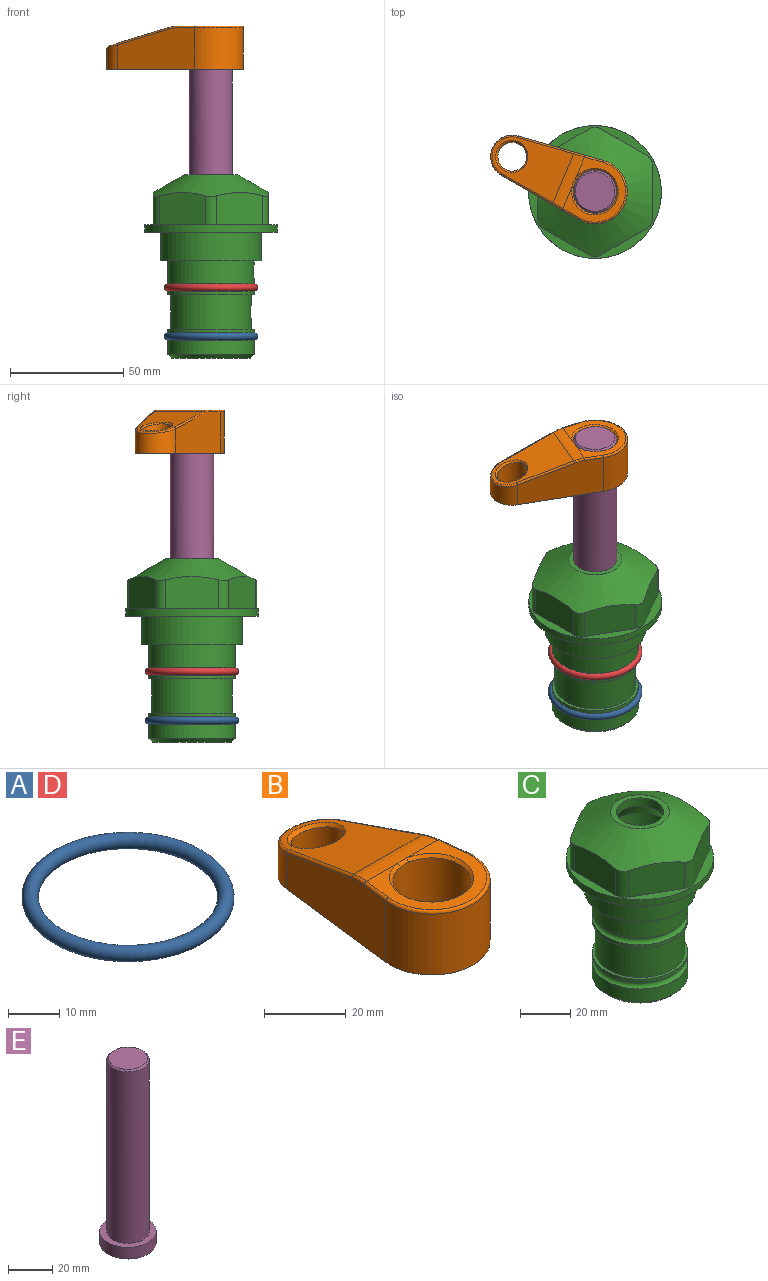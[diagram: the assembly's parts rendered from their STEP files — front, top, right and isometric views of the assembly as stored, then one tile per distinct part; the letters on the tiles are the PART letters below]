
ASSEMBLY  parts=5 mates=4
PART A: 1 faces, bbox 44.7x44.7x3.2 mm
  f0: torus R=19.05mm, axis (0,0,1), area 1193.9mm2
PART B: 31 faces, bbox 31.7x65.5x19.8 mm
  f0: plane 39.12x18.26mm, normal (0.99,0.12,0), area 612.2mm2, adj f1,f4,f7,f11,f13,f15
  f1: cylinder r=9.53mm len=18.91mm, axis (0,0,-1), area 296.1mm2, adj f0,f2,f7,f17
  f2: plane 39.12x18.26mm, normal (-0.99,0.12,0), area 612.2mm2, adj f1,f4,f7,f12,f14,f16
  f3: cylinder r=6.35mm len=12.7mm, axis (0,0,-1), area 362.4mm2, adj f7,f18
  f4: cylinder r=14.29mm len=28.58mm, axis (0,0,-1), area 882.2mm2, adj f0,f2,f7,f10
  f5: cylinder r=9.53mm len=19.05mm, axis (0,0,-1), area 1092.6mm2, adj f7,f19,f20
  f6: plane 26.99x23.69mm, normal (0,0,1), area 216.2mm2, adj f9,f10,f11,f12,f19
  f7: plane 63.5x28.58mm, normal (0,0,-1), area 661.8mm2, adj f0,f1,f2,f3,f4,f5,f22,f23
  f8: plane 33.52x23.6mm, normal (0,0.26,0.97), area 486mm2, adj f9,f15,f16,f17,f18
  f9: cylinder r=19.05mm len=24.72mm, axis (1,0,0), area 120.4mm2, adj f6,f8,f13,f14,f20
  f10: torus R=13.49mm, axis (0,0,1), area 59mm2, adj f4,f6,f11,f12
  f11: cylinder r=0.79mm len=8.67mm, axis (0.12,-0.99,0), area 10.8mm2, adj f0,f6,f10,f13
  f12: cylinder r=0.79mm len=8.67mm, axis (0.12,0.99,0), area 10.8mm2, adj f2,f6,f10,f14
  f13: bspline ~4.95x1.42mm, area 6.1mm2, adj f0,f9,f11,f15
  f14: bspline ~4.95x1.42mm, area 6.1mm2, adj f2,f9,f12,f16
  f15: cylinder r=0.79mm len=25.95mm, axis (0.12,-0.96,0.26), area 32.9mm2, adj f0,f8,f13,f17
  f16: cylinder r=0.79mm len=25.95mm, axis (0.12,0.96,-0.26), area 32.9mm2, adj f2,f8,f14,f17
  f17: bspline ~18.91x8.38mm, area 30mm2, adj f1,f8,f15,f16
  f18: bspline ~14.29x14.29mm, area 48.3mm2, adj f3,f8
  f19: cone r=9.53mm half-angle=45deg, axis (0,0,1), area 66.5mm2, adj f5,f6,f20
  f20: bspline ~3.22x0.96mm, area 3.5mm2, adj f5,f9,f19
  f21: plane 2.75x2.72mm, normal (0,0,-1), area 2.9mm2, adj f23,f25,f28
  f22: plane 23.05x15.88mm, normal (-0.99,-0.12,0), area 323.6mm2, adj f7,f25,f26,f27,f28,f29
  f23: plane 23.05x15.88mm, normal (0.99,-0.12,0), area 323.6mm2, adj f7,f21,f25,f27,f28,f30
  f24: cylinder r=9.53mm len=10.69mm, axis (0,0,-1), area 114.7mm2, adj f7,f27,f29,f30
  f25: cylinder r=12.7mm len=20.59mm, axis (0,0,-1), area 381.1mm2, adj f7,f21,f22,f23,f26,f28
  f26: plane 2.75x2.72mm, normal (0,0,-1), area 2.9mm2, adj f22,f25,f28
  f27: plane 19.72x18.37mm, normal (0,-0.26,-0.97), area 291.8mm2, adj f22,f23,f24,f28,f29,f30
  f28: cylinder r=15.88mm len=19.92mm, axis (1,0,0), area 54.8mm2, adj f21,f22,f23,f25,f26,f27
  f29: cylinder r=1.59mm len=11mm, axis (0,0,-1), area 34.7mm2, adj f7,f22,f24,f27
  f30: cylinder r=1.59mm len=11mm, axis (0,0,-1), area 34.7mm2, adj f7,f23,f24,f27
PART C: 36 faces, bbox 58.7x58.7x81 mm
  f0: cylinder r=17.78mm len=35.56mm, axis (0,0,1), area 1670.8mm2, adj f23,f24,f31
  f1: cylinder r=19.05mm len=38.1mm, axis (0,0,1), area 1191.9mm2, adj f26,f27,f30
  f2: plane 58.66x58.66mm, normal (0,0,-1), area 1150.6mm2, adj f3,f28
  f3: cylinder r=29.33mm len=58.66mm, axis (0,0,-1), area 585.1mm2, adj f2,f4
  f4: plane 58.66x58.66mm, normal (0,0,1), area 475.9mm2, adj f3,f5,f6,f7,f8,f9,f10,f11
  f5: plane 20.32x14.34mm, normal (-0.5,0.87,0), area 324.4mm2, adj f4,f15,f16,f17
  f6: plane 20.32x14.34mm, normal (0.5,0.87,0), area 324.4mm2, adj f4,f14,f15,f17
  f7: plane 23.48x14.34mm, normal (1,0,0), area 324.4mm2, adj f4,f13,f14,f17
  f8: plane 20.32x14.34mm, normal (0.5,-0.87,0), area 324.4mm2, adj f4,f12,f13,f17
  f9: plane 20.32x14.34mm, normal (-0.5,-0.87,0), area 324.4mm2, adj f4,f11,f12,f17
  f10: plane 23.48x14.34mm, normal (-1,0,0), area 324.4mm2, adj f4,f11,f16,f17
  f11: cylinder r=5.08mm len=12.85mm, axis (0,0,-1), area 67.2mm2, adj f4,f9,f10,f17
  f12: cylinder r=5.08mm len=12.85mm, axis (0,0,-1), area 67.2mm2, adj f4,f8,f9,f17
  f13: cylinder r=5.08mm len=12.85mm, axis (0,0,-1), area 67.2mm2, adj f4,f7,f8,f17
  f14: cylinder r=5.08mm len=12.85mm, axis (0,0,-1), area 67.2mm2, adj f4,f6,f7,f17
  f15: cylinder r=5.08mm len=12.85mm, axis (0,0,-1), area 67.2mm2, adj f4,f5,f6,f17
  f16: cylinder r=5.08mm len=12.85mm, axis (0,0,-1), area 67.2mm2, adj f4,f5,f10,f17
  f17: cone r=11.73mm half-angle=60deg, axis (0,0,-1), area 2071.8mm2, adj f5,f6,f7,f8,f9,f10,f11,f12
  f18: plane 23.46x23.46mm, normal (0,0,1), area 147.4mm2, adj f17,f35
  f19: plane 34.93x34.93mm, normal (0,0,-1), area 958mm2, adj f29
  f20: cylinder r=19.05mm len=38.1mm, axis (0,0,1), area 760.1mm2, adj f21,f29
  f21: torus R=19.05mm, axis (0,0,1), area 565.3mm2, adj f20,f22
  f22: cylinder r=19.05mm len=38.1mm, axis (0,0,1), area 190mm2, adj f21,f23
  f23: plane 38.1x38.1mm, normal (0,0,1), area 146.9mm2, adj f0,f22
  f24: plane 38.1x38.1mm, normal (0,0,-1), area 146.9mm2, adj f0,f25
  f25: cylinder r=19.05mm len=38.1mm, axis (0,0,1), area 190mm2, adj f24,f26
  f26: torus R=19.05mm, axis (0,0,1), area 565.3mm2, adj f1,f25
  f27: plane 44.45x44.45mm, normal (0,0,-1), area 411.7mm2, adj f1,f28
  f28: cylinder r=22.23mm len=44.45mm, axis (0,0,1), area 1773.5mm2, adj f2,f27
  f29: cone r=19.05mm half-angle=45deg, axis (0,0,1), area 257.5mm2, adj f19,f20
  f30: cylinder r=3.17mm len=6.75mm, axis (-1,0,0), area 128mm2, adj f1,f33
  f31: cylinder r=3.17mm len=6.35mm, axis (-1,0,0), area 102.5mm2, adj f0,f33
  f32: plane 25.4x25.4mm, normal (0,0,1), area 506.7mm2, adj f33
  f33: cylinder r=12.7mm len=66.42mm, axis (0,0,-1), area 5236.2mm2, adj f30,f31,f32,f34
  f34: cone r=9.53mm half-angle=30deg, axis (0,0,-1), area 443.4mm2, adj f33,f35
  f35: cylinder r=9.53mm len=19.05mm, axis (0,0,-1), area 240.9mm2, adj f18,f34
PART D: same geometry as A
PART E: 6 faces, bbox 25.4x25.4x101.6 mm
  f0: plane 17.46x17.46mm, normal (0,0,1), area 239.5mm2, adj f5
  f1: plane 25.4x25.4mm, normal (0,0,-1), area 506.7mm2, adj f2
  f2: cylinder r=12.7mm len=25.4mm, axis (0,0,1), area 506.7mm2, adj f1,f3
  f3: plane 25.4x25.4mm, normal (0,0,1), area 221.7mm2, adj f2,f4
  f4: cylinder r=9.53mm len=94.46mm, axis (0,0,1), area 5653mm2, adj f3,f5
  f5: cone r=8.73mm half-angle=45deg, axis (0,0,-1), area 64.4mm2, adj f0,f4
PLACE A t=(0,0,-21.59)mm
PLACE B rot(axis=(0,0,1),67.1deg) t=(0,0,27.55)mm
PLACE C at identity fixed
PLACE D at identity
PLACE E rot(axis=(0,0,1),67.1deg) t=(0,0,27.55)mm
MATE fastened B.f4 <-> E.f2  axis (0,0,1) through (0,0,91.05)mm
MATE fastened A.f0 <-> C.f0  axis (0,0,1) through (0,0,-46.1)mm
MATE fastened D.f0 <-> C.f0  axis (0,0,1) through (0,0,-24.51)mm
MATE cylindrical E.f2 <-> C.f0  axis (0,0,-1) through (0,0,-10.55)mm
